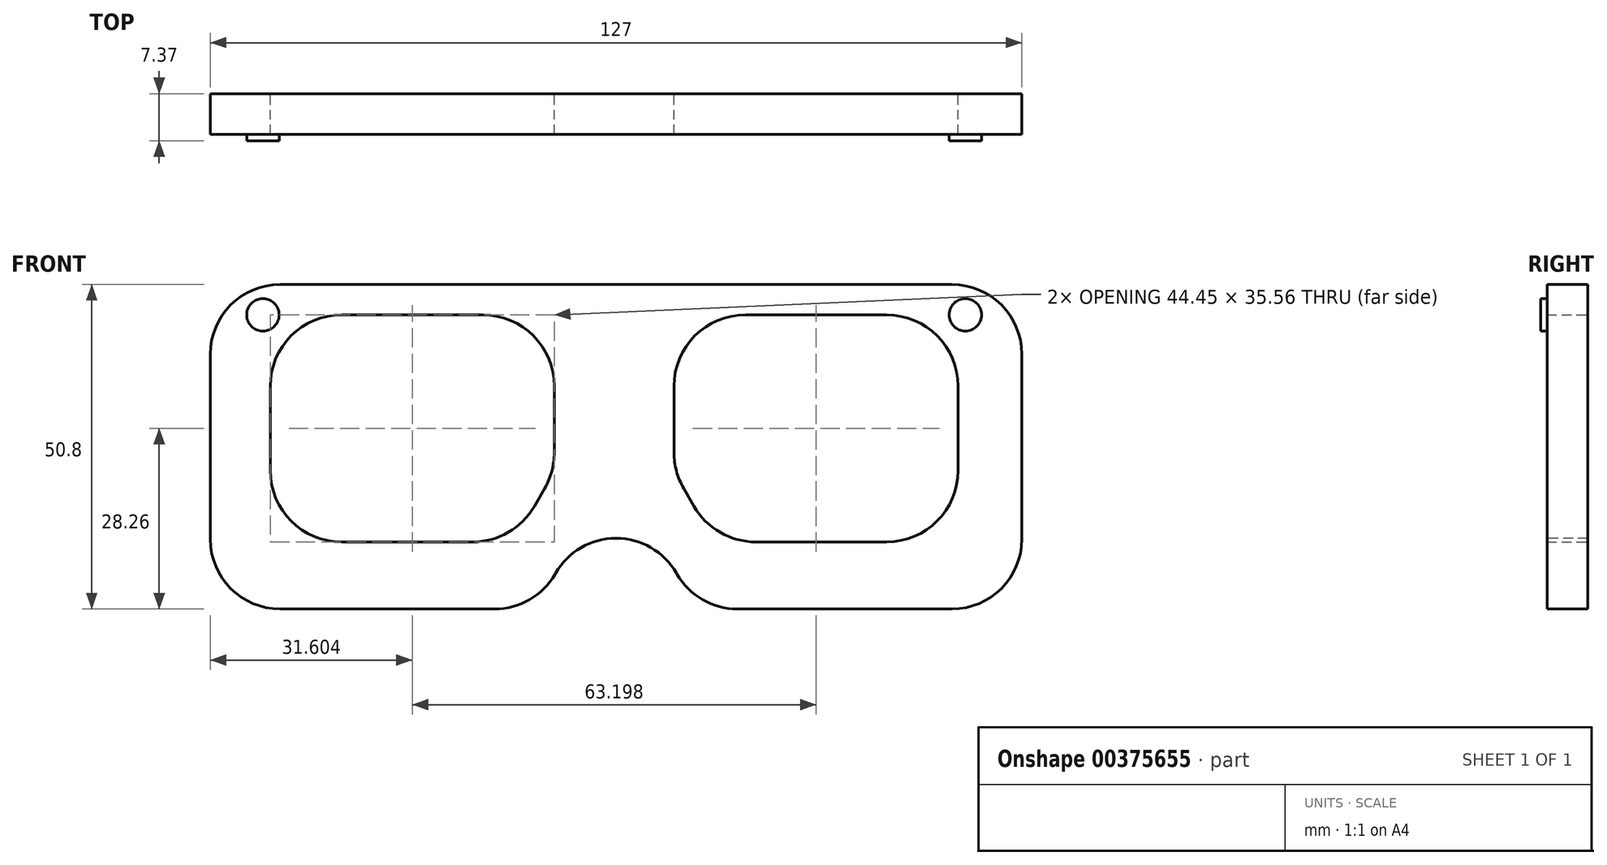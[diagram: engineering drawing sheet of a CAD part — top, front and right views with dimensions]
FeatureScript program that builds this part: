
annotation { "Feature Type Name" : "Feature", "Feature Type Description" : "" }
export const myFeature = defineFeature(function(context is Context, id is Id, definition is map)
    precondition{}
    {
        {
            var Q0;
            Q0=qCreatedBy(makeId("Front.planeOp"),FACE);
            var sketch = newSketch(context, id + "F0", { "sketchPlane" : qUnion([Q0])});
            skLineSegment(sketch, "E0", {"start": v(-63.5, 40.32) * mm, "end": v(63.5, 40.32) * mm});
            skLineSegment(sketch, "E1", {"start": v(63.5, 40.32) * mm, "end": v(63.5, -10.48) * mm});
            skLineSegment(sketch, "E2", {"start": v(63.5, -10.48) * mm, "end": v(12.7, -10.48) * mm});
            skLineSegment(sketch, "E3", {"start": v(12.7, -10.48) * mm, "end": v(0, 11.51) * mm});
            skLineSegment(sketch, "E4", {"start": v(0, 11.51) * mm, "end": v(-12.7, -10.48) * mm});
            skLineSegment(sketch, "E5", {"start": v(-12.7, -10.48) * mm, "end": v(-63.5, -10.48) * mm});
            skLineSegment(sketch, "E6", {"start": v(-63.5, -10.48) * mm, "end": v(-63.5, 40.32) * mm});
            skSolve(sketch);
        }
        {
            var Q0;
            Q0 = qSketchRegion(id + "F0", true);
            extrude(context, id + "F1", {"entities" : qUnion([Q0]), "depth" : 6.35 * mm});
        }
        {
            var Q0;
            Q0=makeQuery(id+"F1.opExtrude","SWEPT_EDGE",EDGE,{"disambiguationData":[OSD([sQuery(id+"F0.wireOp",EDGE,"E0"),sQuery(id+"F0.wireOp",EDGE,"E1")])]});
            var Q1;
            Q1=makeQuery(id+"F1.opExtrude","SWEPT_EDGE",EDGE,{"disambiguationData":[OSD([sQuery(id+"F0.wireOp",EDGE,"E0"),sQuery(id+"F0.wireOp",EDGE,"E6")])]});
            var Q2;
            Q2=makeQuery(id+"F1.opExtrude","SWEPT_EDGE",EDGE,{"disambiguationData":[OSD([sQuery(id+"F0.wireOp",EDGE,"E5"),sQuery(id+"F0.wireOp",EDGE,"E6")])]});
            var Q3;
            Q3=makeQuery(id+"F1.opExtrude","SWEPT_EDGE",EDGE,{"disambiguationData":[OSD([sQuery(id+"F0.wireOp",EDGE,"E4"),sQuery(id+"F0.wireOp",EDGE,"E5")])]});
            var Q4;
            Q4=makeQuery(id+"F1.opExtrude","SWEPT_EDGE",EDGE,{"disambiguationData":[OSD([sQuery(id+"F0.wireOp",EDGE,"E3"),sQuery(id+"F0.wireOp",EDGE,"E4")])]});
            var Q5;
            Q5=makeQuery(id+"F1.opExtrude","SWEPT_EDGE",EDGE,{"disambiguationData":[OSD([sQuery(id+"F0.wireOp",EDGE,"E2"),sQuery(id+"F0.wireOp",EDGE,"E3")])]});
            var Q6;
            Q6=makeQuery(id+"F1.opExtrude","SWEPT_EDGE",EDGE,{"disambiguationData":[OSD([sQuery(id+"F0.wireOp",EDGE,"E1"),sQuery(id+"F0.wireOp",EDGE,"E2")])]});
            fillet(context, id + "F2", {"entities" : qUnion([Q0, Q1, Q2, Q3, Q4, Q5, Q6]), "radius" : 10.92 * mm, "tangentPropagation" : true, "allowEdgeOverflow" : false});
        }
        {
            var Q0;
            Q0=qCreatedBy(makeId("Front.planeOp"),FACE);
            var sketch = newSketch(context, id + "F3", { "sketchPlane" : qUnion([Q0])});
            skLineSegment(sketch, "E7", {"start": v(-54.12, 35.56) * mm, "end": v(-54.12, 0) * mm});
            skLineSegment(sketch, "E8", {"start": v(-54.12, 0) * mm, "end": v(-16.02, 0) * mm});
            skLineSegment(sketch, "E9", {"start": v(-16.02, 0) * mm, "end": v(-9.67, 11) * mm});
            skLineSegment(sketch, "E10", {"start": v(-9.67, 11) * mm, "end": v(-9.67, 35.56) * mm});
            skLineSegment(sketch, "E11", {"start": v(-9.67, 35.56) * mm, "end": v(-54.12, 35.56) * mm});
            skLineSegment(sketch, "E12", {"start": v(9.08, 35.56) * mm, "end": v(9.08, 11) * mm});
            skLineSegment(sketch, "E13", {"start": v(9.08, 11) * mm, "end": v(15.43, 0) * mm});
            skLineSegment(sketch, "E14", {"start": v(15.43, 0) * mm, "end": v(53.53, 0) * mm});
            skLineSegment(sketch, "E15", {"start": v(53.53, 0) * mm, "end": v(53.53, 35.56) * mm});
            skLineSegment(sketch, "E16", {"start": v(53.53, 35.56) * mm, "end": v(9.08, 35.56) * mm});
            skSolve(sketch);
        }
        {
            var Q0;
            Q0 = qSketchRegion(id + "F3", true);
            extrude(context, id + "F4", {"entities" : qUnion([Q0]), "operationType" : NewBodyOperationType.REMOVE, "depth" : 25.4 * mm});
        }
        {
            var Q0;
            Q0=makeQuery(id+"F4.boolean.opBoolean","COPY",EDGE,{"derivedFrom":makeQuery(id+"F4.opExtrude","SWEPT_EDGE",EDGE,{"disambiguationData":[OSD([sQuery(id+"F3.wireOp",EDGE,"E7"),sQuery(id+"F3.wireOp",EDGE,"E11")])]})});
            var Q1;
            Q1=makeQuery(id+"F4.boolean.opBoolean","COPY",EDGE,{"derivedFrom":makeQuery(id+"F4.opExtrude","SWEPT_EDGE",EDGE,{"disambiguationData":[OSD([sQuery(id+"F3.wireOp",EDGE,"E10"),sQuery(id+"F3.wireOp",EDGE,"E11")])]})});
            var Q2;
            Q2=makeQuery(id+"F4.boolean.opBoolean","COPY",EDGE,{"derivedFrom":makeQuery(id+"F4.opExtrude","SWEPT_EDGE",EDGE,{"disambiguationData":[OSD([sQuery(id+"F3.wireOp",EDGE,"E9"),sQuery(id+"F3.wireOp",EDGE,"E10")])]})});
            var Q3;
            Q3=makeQuery(id+"F4.boolean.opBoolean","COPY",EDGE,{"derivedFrom":makeQuery(id+"F4.opExtrude","SWEPT_EDGE",EDGE,{"disambiguationData":[OSD([sQuery(id+"F3.wireOp",EDGE,"E8"),sQuery(id+"F3.wireOp",EDGE,"E9")])]})});
            var Q4;
            Q4=makeQuery(id+"F4.boolean.opBoolean","COPY",EDGE,{"derivedFrom":makeQuery(id+"F4.opExtrude","SWEPT_EDGE",EDGE,{"disambiguationData":[OSD([sQuery(id+"F3.wireOp",EDGE,"E7"),sQuery(id+"F3.wireOp",EDGE,"E8")])]})});
            var Q5;
            Q5=makeQuery(id+"F4.boolean.opBoolean","COPY",EDGE,{"derivedFrom":makeQuery(id+"F4.opExtrude","SWEPT_EDGE",EDGE,{"disambiguationData":[OSD([sQuery(id+"F3.wireOp",EDGE,"E13"),sQuery(id+"F3.wireOp",EDGE,"E14")])]})});
            var Q6;
            Q6=makeQuery(id+"F4.boolean.opBoolean","COPY",EDGE,{"derivedFrom":makeQuery(id+"F4.opExtrude","SWEPT_EDGE",EDGE,{"disambiguationData":[OSD([sQuery(id+"F3.wireOp",EDGE,"E12"),sQuery(id+"F3.wireOp",EDGE,"E13")])]})});
            var Q7;
            Q7=makeQuery(id+"F4.boolean.opBoolean","COPY",EDGE,{"derivedFrom":makeQuery(id+"F4.opExtrude","SWEPT_EDGE",EDGE,{"disambiguationData":[OSD([sQuery(id+"F3.wireOp",EDGE,"E12"),sQuery(id+"F3.wireOp",EDGE,"E16")])]})});
            var Q8;
            Q8=makeQuery(id+"F4.boolean.opBoolean","COPY",EDGE,{"derivedFrom":makeQuery(id+"F4.opExtrude","SWEPT_EDGE",EDGE,{"disambiguationData":[OSD([sQuery(id+"F3.wireOp",EDGE,"E15"),sQuery(id+"F3.wireOp",EDGE,"E16")])]})});
            var Q9;
            Q9=makeQuery(id+"F4.boolean.opBoolean","COPY",EDGE,{"derivedFrom":makeQuery(id+"F4.opExtrude","SWEPT_EDGE",EDGE,{"disambiguationData":[OSD([sQuery(id+"F3.wireOp",EDGE,"E14"),sQuery(id+"F3.wireOp",EDGE,"E15")])]})});
            fillet(context, id + "F5", {"entities" : qUnion([Q0, Q1, Q2, Q3, Q4, Q5, Q6, Q7, Q8, Q9]), "radius" : 11.18 * mm, "tangentPropagation" : true, "allowEdgeOverflow" : false});
        }
        {
            var Q0;
            Q0=qCreatedBy(makeId("Front.planeOp"),FACE);
            var sketch = newSketch(context, id + "F6", { "sketchPlane" : qUnion([Q0])});
            skLineSegment(sketch, "E17.0", {"start": v(-54.12, 11.18) * mm, "end": v(-54.12, 24.38) * mm});
            skArc(sketch, "E18.0", {"start": v(-54.12, 24.38) * mm, "mid": v(-50.85, 32.29) * mm, "end": v(-42.95, 35.56) * mm});
            skLineSegment(sketch, "E19.0", {"start": v(-42.95, 35.56) * mm, "end": v(-20.85, 35.56) * mm});
            skArc(sketch, "E20.0", {"start": v(-20.85, 35.56) * mm, "mid": v(-12.94, 32.29) * mm, "end": v(-9.67, 24.38) * mm});
            skLineSegment(sketch, "E21.0", {"start": v(-9.67, 24.38) * mm, "end": v(-9.67, 14) * mm});
            skArc(sketch, "E22.0", {"start": v(-9.67, 14) * mm, "mid": v(-10.05, 11.1) * mm, "end": v(-11.17, 8.4) * mm});
            skLineSegment(sketch, "E23.0", {"start": v(-11.17, 8.4) * mm, "end": v(-12.8, 5.59) * mm});
            skArc(sketch, "E24.0", {"start": v(-12.8, 5.59) * mm, "mid": v(-16.89, 1.5) * mm, "end": v(-22.47, 0) * mm});
            skArc(sketch, "E25.0", {"start": v(-42.95, 0) * mm, "mid": v(-50.85, 3.27) * mm, "end": v(-54.12, 11.18) * mm});
            skLineSegment(sketch, "E25.1", {"start": v(-22.47, 0) * mm, "end": v(-42.95, 0) * mm});
            skLineSegment(sketch, "E26.0", {"start": v(9.08, 14) * mm, "end": v(9.08, 24.38) * mm});
            skArc(sketch, "E27.0", {"start": v(10.57, 8.4) * mm, "mid": v(9.46, 11.1) * mm, "end": v(9.08, 14) * mm});
            skLineSegment(sketch, "E28.0", {"start": v(12.2, 5.59) * mm, "end": v(10.57, 8.4) * mm});
            skArc(sketch, "E29.0", {"start": v(21.88, 0) * mm, "mid": v(16.3, 1.5) * mm, "end": v(12.2, 5.59) * mm});
            skLineSegment(sketch, "E30.0", {"start": v(42.35, 0) * mm, "end": v(21.88, 0) * mm});
            skArc(sketch, "E31.0", {"start": v(53.53, 11.18) * mm, "mid": v(50.25, 3.27) * mm, "end": v(42.35, 0) * mm});
            skLineSegment(sketch, "E32.0", {"start": v(53.53, 11.18) * mm, "end": v(53.53, 24.38) * mm});
            skArc(sketch, "E33.0", {"start": v(53.53, 24.38) * mm, "mid": v(50.25, 32.29) * mm, "end": v(42.35, 35.56) * mm});
            skLineSegment(sketch, "E34.0", {"start": v(42.35, 35.56) * mm, "end": v(20.25, 35.56) * mm});
            skArc(sketch, "E35.0", {"start": v(9.08, 24.38) * mm, "mid": v(12.35, 32.29) * mm, "end": v(20.25, 35.56) * mm});
            skSolve(sketch);
        }
        {
            var Q0;
            Q0 = qSketchRegion(id + "F6", true);
            extrude(context, id + "F7", {"entities" : qUnion([Q0]), "depth" : 6.35 * mm});
        }
        {
            var Q0;
            Q0=makeQuery(id+"F1.opExtrude","CAP_FACE",FACE,{"disambiguationData":[OSD([sQuery(id+"F0.wireOp",EDGE,"E0"),sQuery(id+"F0.wireOp",EDGE,"E1"),sQuery(id+"F0.wireOp",EDGE,"E2"),sQuery(id+"F0.wireOp",EDGE,"E3"),sQuery(id+"F0.wireOp",EDGE,"E4"),sQuery(id+"F0.wireOp",EDGE,"E5"),sQuery(id+"F0.wireOp",EDGE,"E6")])],"isStart":false});
            var sketch = newSketch(context, id + "F8", { "sketchPlane" : qUnion([Q0])});
            skCircle(sketch, "E36", {"center": v(54.67, 35.56) * mm, "radius": 2.54 * mm});
            skPoint(sketch, "E36.centerSnap0", {"position": v(31.3, 35.56) * mm});
            skCircle(sketch, "E37", {"center": v(-55.27, 35.56) * mm, "radius": 2.54 * mm});
            skPoint(sketch, "E37.perimeterSnap0", {"position": v(-60.3, 37.12) * mm});
            skPoint(sketch, "E37.perimeterSnap1", {"position": v(-50.85, 32.29) * mm});
            skSolve(sketch);
        }
        {
            var Q0;
            Q0 = qSketchRegion(id + "F8", true);
            extrude(context, id + "F9", {"entities" : qUnion([Q0]), "depth" : 1.02 * mm});
        }
    });
